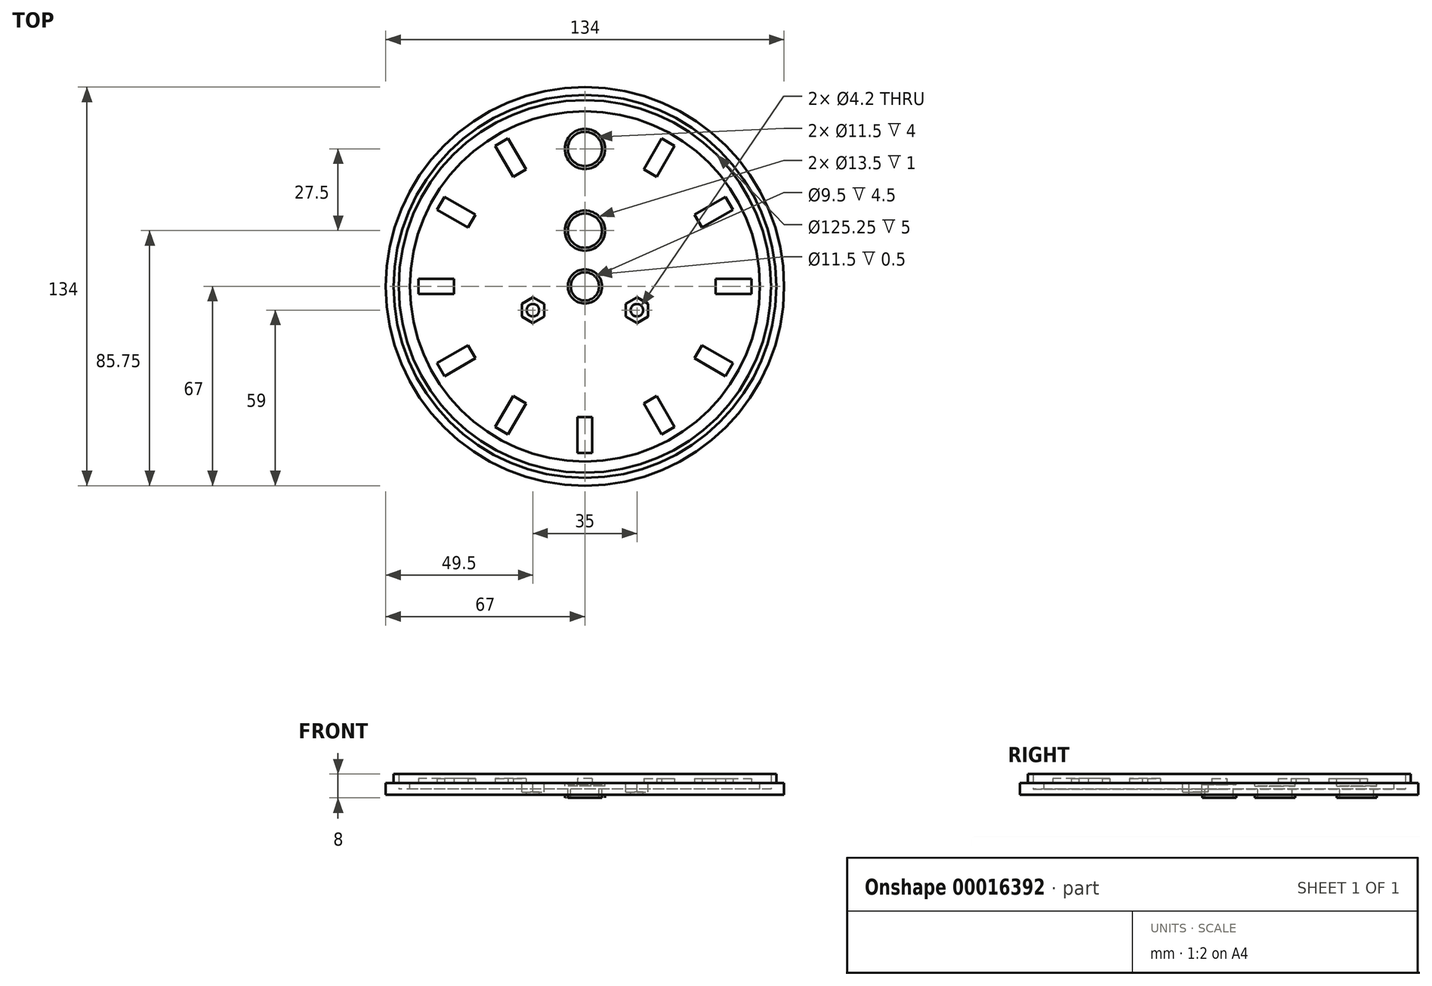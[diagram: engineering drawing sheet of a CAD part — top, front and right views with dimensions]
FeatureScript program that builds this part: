
annotation { "Feature Type Name" : "Feature", "Feature Type Description" : "" }
export const myFeature = defineFeature(function(context is Context, id is Id, definition is map)
    precondition{}
    {
        {
            var Q0;
            Q0=qCreatedBy(makeId("Top.planeOp"),FACE);
            var sketch = newSketch(context, id + "F0", { "sketchPlane" : qUnion([Q0])});
            skCircle(sketch, "E0", {"center": v(0, 0) * mm, "radius": 67 * mm});
            skSolve(sketch);
        }
        {
            var Q0;
            Q0 = qSketchRegion(id + "F0", true);
            var Q1;
            Q1=sQuery(id+"F0.wireOp",EDGE,"E0");
            extrude(context, id + "F1", {"entities" : qUnion([Q0]), "surfaceEntities" : qUnion([Q1]), "endBound" : BoundingType.SYMMETRIC, "depth" : 5 * mm});
        }
        {
            var Q0;
            Q0=makeQuery(id+"F1.opExtrude","CAP_FACE",FACE,{"disambiguationData":[OSD([sQuery(id+"F0.wireOp",EDGE,"E0")])],"isStart":false});
            var sketch = newSketch(context, id + "F2", { "sketchPlane" : qUnion([Q0])});
            skCircle(sketch, "E1", {"center": v(0, 0) * mm, "radius": 63.5 * mm, "construction": true});
            skCircle(sketch, "E2", {"center": v(0, 0) * mm, "radius": 64.38 * mm});
            skCircle(sketch, "E3", {"center": v(0, 0) * mm, "radius": 62.62 * mm});
            skLineSegment(sketch, "E4", {"start": v(0, 62.62) * mm, "end": v(0, 63.5) * mm, "construction": true});
            skLineSegment(sketch, "E5", {"start": v(0, 63.5) * mm, "end": v(0, 64.38) * mm, "construction": true});
            skCircle(sketch, "E6.0", {"center": v(0, 0) * mm, "radius": 58.88 * mm});
            skSolve(sketch);
        }
        {
            var Q0;
            Q0=makeQuery(id+"F2.imprint","IMPRINT",FACE,{"disambiguationData":[TD([[makeQuery(id+"F2.imprint","IMPRINT",EDGE,{"derivedFrom":sQuery(id+"F2.wireOp",EDGE,"E2")}),1.0]])]});
            extrude(context, id + "F3", {"entities" : qUnion([Q0]), "operationType" : NewBodyOperationType.ADD, "depth" : 3 * mm});
        }
        {
            var Q0;
            Q0=makeQuery(id+"F2.imprint","IMPRINT",FACE,{"disambiguationData":[TD([[makeQuery(id+"F2.imprint","IMPRINT",EDGE,{"derivedFrom":sQuery(id+"F2.wireOp",EDGE,"E3")}),1.0]])]});
            extrude(context, id + "F4", {"entities" : qUnion([Q0]), "operationType" : NewBodyOperationType.REMOVE, "oppositeDirection" : true, "depth" : 2 * mm});
        }
        {
            var Q0;
            Q0=makeQuery(id+"F3.boolean.opBoolean","SPLIT",FACE,{"disambiguationData":[TD([makeQuery(id+"F3.opExtrude","SWEPT_FACE",FACE,{"disambiguationData":[OSD([sQuery(id+"F2.wireOp",EDGE,"E3")])]})])],"derivedFrom":makeQuery(id+"F1.opExtrude","CAP_FACE",FACE,{"disambiguationData":[OSD([sQuery(id+"F0.wireOp",EDGE,"E0")])],"isStart":false})});
            var sketch = newSketch(context, id + "F5", { "sketchPlane" : qUnion([Q0])});
            skCircle(sketch, "E7", {"center": v(0, 0) * mm, "radius": 4.75 * mm});
            skCircle(sketch, "E8", {"center": v(0, 18.75) * mm, "radius": 5.75 * mm});
            skCircle(sketch, "E9", {"center": v(0, 46.25) * mm, "radius": 5.75 * mm});
            skCircle(sketch, "E10", {"center": v(-17.5, -8) * mm, "radius": 2.1 * mm});
            skCircle(sketch, "E11", {"center": v(17.5, -8) * mm, "radius": 2.1 * mm});
            skLineSegment(sketch, "E12", {"start": v(-17.5, -8) * mm, "end": v(17.5, -8) * mm, "construction": true});
            skLineSegment(sketch, "E13", {"start": v(0, 0) * mm, "end": v(0, -8) * mm, "construction": true});
            skSolve(sketch);
        }
        {
            var Q0;
            Q0 = qSketchRegion(id + "F5", true);
            extrude(context, id + "F6", {"entities" : qUnion([Q0]), "operationType" : NewBodyOperationType.REMOVE, "endBound" : BoundingType.THROUGH_ALL, "oppositeDirection" : true, "depth" : 25 * mm});
        }
        {
            var Q0;
            Q0=makeQuery(id+"F3.boolean.opBoolean","SPLIT",FACE,{"disambiguationData":[TD([makeQuery(id+"F3.opExtrude","SWEPT_FACE",FACE,{"disambiguationData":[OSD([sQuery(id+"F2.wireOp",EDGE,"E3")])]})])],"derivedFrom":makeQuery(id+"F1.opExtrude","CAP_FACE",FACE,{"disambiguationData":[OSD([sQuery(id+"F0.wireOp",EDGE,"E0")])],"isStart":false})});
            var sketch = newSketch(context, id + "F7", { "sketchPlane" : qUnion([Q0])});
            skCircle(sketch, "E14.0", {"center": v(0, 46.25) * mm, "radius": 6.75 * mm});
            skCircle(sketch, "E15.0", {"center": v(0, 18.75) * mm, "radius": 6.75 * mm});
            skCircle(sketch, "E16.0", {"center": v(0, 0) * mm, "radius": 5.75 * mm});
            skCircle(sketch, "E17.cCircle", {"center": v(17.5, -8) * mm, "radius": 3.75 * mm, "construction": true});
            skLineSegment(sketch, "E17.0", {"start": v(21.25, -5.83) * mm, "end": v(21.25, -10.17) * mm});
            skLineSegment(sketch, "E17.1", {"start": v(21.25, -10.17) * mm, "end": v(17.5, -12.33) * mm});
            skLineSegment(sketch, "E17.2", {"start": v(17.5, -12.33) * mm, "end": v(13.75, -10.17) * mm});
            skLineSegment(sketch, "E17.3", {"start": v(13.75, -10.17) * mm, "end": v(13.75, -5.83) * mm});
            skLineSegment(sketch, "E17.4", {"start": v(13.75, -5.83) * mm, "end": v(17.5, -3.67) * mm});
            skLineSegment(sketch, "E17.5", {"start": v(17.5, -3.67) * mm, "end": v(21.25, -5.83) * mm});
            skPoint(sketch, "E17.0.midPoint", {"position": v(21.25, -8) * mm});
            skCircle(sketch, "E18.cCircle", {"center": v(-17.5, -8) * mm, "radius": 3.75 * mm, "construction": true});
            skLineSegment(sketch, "E18.0", {"start": v(-13.75, -5.83) * mm, "end": v(-13.75, -10.17) * mm});
            skLineSegment(sketch, "E18.1", {"start": v(-13.75, -10.17) * mm, "end": v(-17.5, -12.33) * mm});
            skLineSegment(sketch, "E18.2", {"start": v(-17.5, -12.33) * mm, "end": v(-21.25, -10.17) * mm});
            skLineSegment(sketch, "E18.3", {"start": v(-21.25, -10.17) * mm, "end": v(-21.25, -5.83) * mm});
            skLineSegment(sketch, "E18.4", {"start": v(-21.25, -5.83) * mm, "end": v(-17.5, -3.67) * mm});
            skLineSegment(sketch, "E18.5", {"start": v(-17.5, -3.67) * mm, "end": v(-13.75, -5.83) * mm});
            skPoint(sketch, "E18.0.midPoint", {"position": v(-13.75, -8) * mm});
            skSolve(sketch);
        }
        {
            var Q0;
            Q0=makeQuery(id+"F7.imprint","IMPRINT",FACE,{"disambiguationData":[TD([[makeQuery(id+"F7.imprint","IMPRINT",EDGE,{"derivedFrom":sQuery(id+"F7.wireOp",EDGE,"E16.0")}),1.0]])]});
            extrude(context, id + "F8", {"entities" : qUnion([Q0]), "operationType" : NewBodyOperationType.REMOVE, "oppositeDirection" : true, "depth" : 0.5 * mm});
        }
        {
            var Q0;
            Q0=makeQuery(id+"F7.imprint","IMPRINT",FACE,{"disambiguationData":[TD([[makeQuery(id+"F7.imprint","IMPRINT",EDGE,{"derivedFrom":sQuery(id+"F7.wireOp",EDGE,"E14.0")}),1.0]])]});
            var Q1;
            Q1=makeQuery(id+"F7.imprint","IMPRINT",FACE,{"disambiguationData":[TD([[makeQuery(id+"F7.imprint","IMPRINT",EDGE,{"derivedFrom":sQuery(id+"F7.wireOp",EDGE,"E15.0")}),1.0]])]});
            extrude(context, id + "F9", {"entities" : qUnion([Q0, Q1]), "operationType" : NewBodyOperationType.REMOVE, "oppositeDirection" : true, "depth" : 1 * mm});
        }
        {
            var Q0;
            Q0=makeQuery(id+"F7.imprint","IMPRINT",FACE,{"disambiguationData":[TD([[makeQuery(id+"F7.imprint","IMPRINT",EDGE,{"derivedFrom":sQuery(id+"F7.wireOp",EDGE,"E18.0")}),-1.0]])]});
            var Q1;
            Q1=makeQuery(id+"F7.imprint","IMPRINT",FACE,{"disambiguationData":[TD([[makeQuery(id+"F7.imprint","IMPRINT",EDGE,{"derivedFrom":sQuery(id+"F7.wireOp",EDGE,"E17.0")}),-1.0]])]});
            extrude(context, id + "F10", {"entities" : qUnion([Q0, Q1]), "operationType" : NewBodyOperationType.REMOVE, "oppositeDirection" : true, "depth" : 3 * mm});
        }
        {
            var Q0;
            Q0=makeQuery(id+"F1.opExtrude","CAP_FACE",FACE,{"disambiguationData":[OSD([sQuery(id+"F0.wireOp",EDGE,"E0")])],"isStart":true});
            var sketch = newSketch(context, id + "F11", { "sketchPlane" : qUnion([Q0])});
            skCircle(sketch, "E19.0", {"center": v(0, -46.25) * mm, "radius": 6.75 * mm});
            skCircle(sketch, "E20.0", {"center": v(0, -18.75) * mm, "radius": 6.75 * mm});
            skCircle(sketch, "E21.0", {"center": v(0, 0) * mm, "radius": 5.75 * mm});
            skSolve(sketch);
        }
        {
            var Q0;
            Q0=makeQuery(id+"F11.imprint","IMPRINT",FACE,{"disambiguationData":[TD([[makeQuery(id+"F11.imprint","IMPRINT",EDGE,{"derivedFrom":sQuery(id+"F11.wireOp",EDGE,"E19.0")}),-1.0]])]});
            var Q1;
            Q1=makeQuery(id+"F11.imprint","IMPRINT",FACE,{"disambiguationData":[TD([[makeQuery(id+"F11.imprint","IMPRINT",EDGE,{"derivedFrom":sQuery(id+"F11.wireOp",EDGE,"E20.0")}),-1.0]])]});
            extrude(context, id + "F12", {"entities" : qUnion([Q0, Q1]), "operationType" : NewBodyOperationType.REMOVE, "oppositeDirection" : true, "depth" : 1 * mm});
        }
        {
            var Q0;
            Q0=makeQuery(id+"F5.imprint","IMPRINT",FACE,{"disambiguationData":[TD([[makeQuery(id+"F5.imprint","IMPRINT",EDGE,{"derivedFrom":sQuery(id+"F5.wireOp",EDGE,"E7")}),-1.0]])]});
            var sketch = newSketch(context, id + "F13", { "sketchPlane" : qUnion([Q0])});
            skCircle(sketch, "E22", {"center": v(0, 0) * mm, "radius": 50 * mm, "construction": true});
            skLineSegment(sketch, "E23.rect.bottom", {"start": v(2.5, -44) * mm, "end": v(-2.5, -44) * mm});
            skLineSegment(sketch, "E23.rect.top", {"start": v(2.5, -56) * mm, "end": v(-2.5, -56) * mm});
            skLineSegment(sketch, "E23.rect.left", {"start": v(2.5, -44) * mm, "end": v(2.5, -56) * mm});
            skLineSegment(sketch, "E23.rect.right", {"start": v(-2.5, -44) * mm, "end": v(-2.5, -56) * mm});
            skPoint(sketch, "E23.rect.middle", {"position": v(0, -50) * mm});
            skSolve(sketch);
        }
        {
            var Q0;
            Q0=makeQuery(id+"F13.imprint","IMPRINT",FACE,{"disambiguationData":[TD([[makeQuery(id+"F13.imprint","IMPRINT",EDGE,{"derivedFrom":sQuery(id+"F13.wireOp",EDGE,"E23.rect.bottom")}),1.0]])]});
            extrude(context, id + "F14", {"entities" : qUnion([Q0]), "operationType" : NewBodyOperationType.ADD, "depth" : 1.5 * mm});
        }
        {
            var Q0;
            Q0=makeQuery(id+"F14.opExtrude","CAP_FACE",FACE,{"disambiguationData":[OSD([sQuery(id+"F13.wireOp",EDGE,"E23.rect.bottom"),sQuery(id+"F13.wireOp",EDGE,"E23.rect.top"),sQuery(id+"F13.wireOp",EDGE,"E23.rect.left"),sQuery(id+"F13.wireOp",EDGE,"E23.rect.right")])],"isStart":false});
            var Q1;
            Q1=makeQuery(id+"F14.opExtrude","SWEPT_FACE",FACE,{"disambiguationData":[OSD([sQuery(id+"F13.wireOp",EDGE,"E23.rect.left")])]});
            var Q2;
            Q2=makeQuery(id+"F14.opExtrude","SWEPT_FACE",FACE,{"disambiguationData":[OSD([sQuery(id+"F13.wireOp",EDGE,"E23.rect.bottom")])]});
            var Q3;
            Q3=makeQuery(id+"F14.opExtrude","SWEPT_FACE",FACE,{"disambiguationData":[OSD([sQuery(id+"F13.wireOp",EDGE,"E23.rect.right")])]});
            var Q4;
            Q4=makeQuery(id+"F14.opExtrude","SWEPT_FACE",FACE,{"disambiguationData":[OSD([sQuery(id+"F13.wireOp",EDGE,"E23.rect.top")])]});
            var Q5;
            Q5=sQuery(id+"F5.wireOp",EDGE,"E7");
            circularPattern(context, id + "F15", {"faces" : qUnion([Q0, Q1, Q2, Q3, Q4]), "axis" : qUnion([Q5]), "angle" : 30 * degree, "instanceCount" : 6, "patternType" : PatternType.FACE});
        }
        {
            var Q0;
            Q0=makeQuery(id+"F14.opExtrude","CAP_FACE",FACE,{"disambiguationData":[OSD([sQuery(id+"F13.wireOp",EDGE,"E23.rect.bottom"),sQuery(id+"F13.wireOp",EDGE,"E23.rect.top"),sQuery(id+"F13.wireOp",EDGE,"E23.rect.left"),sQuery(id+"F13.wireOp",EDGE,"E23.rect.right")])],"isStart":false});
            var Q1;
            Q1=makeQuery(id+"F14.opExtrude","SWEPT_FACE",FACE,{"disambiguationData":[OSD([sQuery(id+"F13.wireOp",EDGE,"E23.rect.left")])]});
            var Q2;
            Q2=makeQuery(id+"F14.opExtrude","SWEPT_FACE",FACE,{"disambiguationData":[OSD([sQuery(id+"F13.wireOp",EDGE,"E23.rect.top")])]});
            var Q3;
            Q3=makeQuery(id+"F14.opExtrude","SWEPT_FACE",FACE,{"disambiguationData":[OSD([sQuery(id+"F13.wireOp",EDGE,"E23.rect.right")])]});
            var Q4;
            Q4=makeQuery(id+"F14.opExtrude","SWEPT_FACE",FACE,{"disambiguationData":[OSD([sQuery(id+"F13.wireOp",EDGE,"E23.rect.bottom")])]});
            var Q5;
            Q5=sQuery(id+"F5.wireOp",EDGE,"E7");
            circularPattern(context, id + "F16", {"faces" : qUnion([Q0, Q1, Q2, Q3, Q4]), "axis" : qUnion([Q5]), "angle" : 30 * degree, "instanceCount" : 6, "oppositeDirection" : true, "patternType" : PatternType.FACE});
        }
    });
